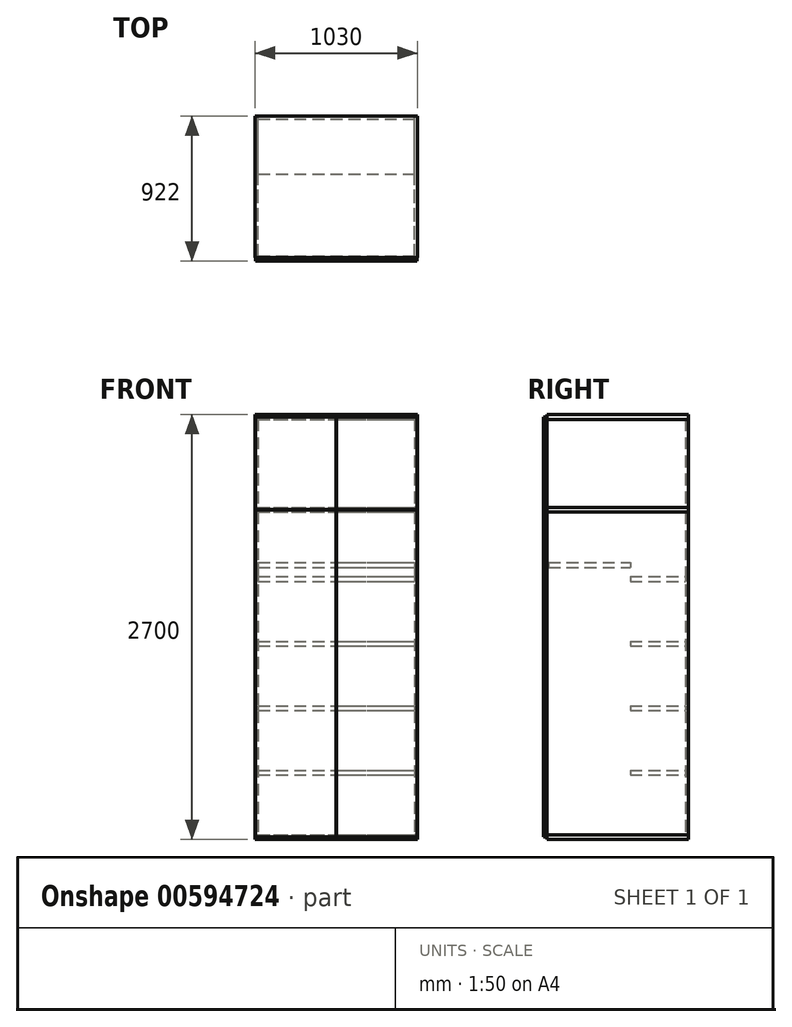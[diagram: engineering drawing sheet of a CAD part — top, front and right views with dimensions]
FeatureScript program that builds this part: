
annotation { "Feature Type Name" : "Feature", "Feature Type Description" : "" }
export const myFeature = defineFeature(function(context is Context, id is Id, definition is map)
    precondition{}
    {
        {
            var Q0;
            Q0=qCreatedBy(makeId("Front.planeOp"),FACE);
            var sketch = newSketch(context, id + "F0", { "sketchPlane" : qUnion([Q0])});
            skLineSegment(sketch, "E0.bottom", {"start": v(515, -1350) * mm, "end": v(-515, -1350) * mm});
            skLineSegment(sketch, "E0.top", {"start": v(515, 1350) * mm, "end": v(-515, 1350) * mm});
            skLineSegment(sketch, "E0.left", {"start": v(515, -1350) * mm, "end": v(515, 1350) * mm});
            skLineSegment(sketch, "E0.right", {"start": v(-515, -1350) * mm, "end": v(-515, 1350) * mm});
            skPoint(sketch, "E0.middle", {"position": v(0, 0) * mm});
            skSolve(sketch);
        }
        {
            var Q0;
            Q0=qCreatedBy(makeId("Front.planeOp"),FACE);
            var sketch = newSketch(context, id + "F1", { "sketchPlane" : qUnion([Q0])});
            skLineSegment(sketch, "E1.bottom", {"start": v(-515, -1350) * mm, "end": v(515, -1350) * mm});
            skLineSegment(sketch, "E1.top", {"start": v(-515, -1320) * mm, "end": v(515, -1320) * mm});
            skLineSegment(sketch, "E1.left", {"start": v(-515, -1350) * mm, "end": v(-515, -1320) * mm});
            skLineSegment(sketch, "E1.right", {"start": v(515, -1350) * mm, "end": v(515, -1320) * mm});
            skLineSegment(sketch, "E2.bottom", {"start": v(-515, 730) * mm, "end": v(515, 730) * mm});
            skLineSegment(sketch, "E2.top", {"start": v(-515, 760) * mm, "end": v(515, 760) * mm});
            skLineSegment(sketch, "E2.left", {"start": v(-515, 730) * mm, "end": v(-515, 760) * mm});
            skLineSegment(sketch, "E2.right", {"start": v(515, 730) * mm, "end": v(515, 760) * mm});
            skLineSegment(sketch, "E3.bottom", {"start": v(-515, 1320) * mm, "end": v(515, 1320) * mm});
            skLineSegment(sketch, "E3.top", {"start": v(-515, 1350) * mm, "end": v(515, 1350) * mm});
            skLineSegment(sketch, "E3.left", {"start": v(-515, 1320) * mm, "end": v(-515, 1350) * mm});
            skLineSegment(sketch, "E3.right", {"start": v(515, 1320) * mm, "end": v(515, 1350) * mm});
            skSolve(sketch);
        }
        {
            var Q0;
            Q0 = qSketchRegion(id + "F1", true);
            extrude(context, id + "F2", {"entities" : qUnion([Q0]), "depth" : 900 * mm, "offsetDistance" : 25 * mm});
        }
        {
            var Q0;
            Q0=qCreatedBy(makeId("Front.planeOp"),FACE);
            var sketch = newSketch(context, id + "F3", { "sketchPlane" : qUnion([Q0])});
            skLineSegment(sketch, "E4", {"start": v(0, 0) * mm, "end": v(0, 1355.76) * mm, "construction": true});
            skLineSegment(sketch, "E5.bottom", {"start": v(-515, 1320) * mm, "end": v(-496, 1320) * mm});
            skLineSegment(sketch, "E5.top", {"start": v(-515, 760) * mm, "end": v(-496, 760) * mm});
            skLineSegment(sketch, "E5.left", {"start": v(-515, 1320) * mm, "end": v(-515, 760) * mm});
            skLineSegment(sketch, "E5.right", {"start": v(-496, 1320) * mm, "end": v(-496, 760) * mm});
            skLineSegment(sketch, "E6.bottom", {"start": v(-515, 730) * mm, "end": v(-496, 730) * mm});
            skLineSegment(sketch, "E6.top", {"start": v(-515, -1320) * mm, "end": v(-496, -1320) * mm});
            skLineSegment(sketch, "E6.left", {"start": v(-515, 730) * mm, "end": v(-515, -1320) * mm});
            skLineSegment(sketch, "E6.right", {"start": v(-496, 730) * mm, "end": v(-496, -1320) * mm});
            skLineSegment(sketch, "E7.MirrorCS", {"start": v(515, -1320) * mm, "end": v(496, -1320) * mm});
            skLineSegment(sketch, "E8.MirrorCS", {"start": v(515, 1320) * mm, "end": v(496, 1320) * mm});
            skLineSegment(sketch, "E9.MirrorCS", {"start": v(515, 760) * mm, "end": v(496, 760) * mm});
            skLineSegment(sketch, "E10.MirrorCS", {"start": v(515, 730) * mm, "end": v(496, 730) * mm});
            skLineSegment(sketch, "E11.MirrorCS", {"start": v(496, 730) * mm, "end": v(496, -1320) * mm});
            skLineSegment(sketch, "E12.MirrorCS", {"start": v(515, 730) * mm, "end": v(515, -1320) * mm});
            skLineSegment(sketch, "E13.MirrorCS", {"start": v(496, 1320) * mm, "end": v(496, 760) * mm});
            skLineSegment(sketch, "E14.MirrorCS", {"start": v(515, 1320) * mm, "end": v(515, 760) * mm});
            skSolve(sketch);
        }
        {
            var Q0;
            Q0 = qSketchRegion(id + "F3", true);
            var Q1;
            Q1=makeQuery(id+"F2.opExtrude","CAP_FACE",FACE,{"disambiguationData":[OSD([sQuery(id+"F1.wireOp",EDGE,"E1.bottom"),sQuery(id+"F1.wireOp",EDGE,"E1.top"),sQuery(id+"F1.wireOp",EDGE,"E1.left"),sQuery(id+"F1.wireOp",EDGE,"E1.right")])],"isStart":false});
            extrude(context, id + "F4", {"entities" : qUnion([Q0]), "endBound" : BoundingType.UP_TO_SURFACE, "depth" : 25 * mm, "endBoundEntityFace" : qUnion([Q1]), "offsetDistance" : 25 * mm});
        }
        {
            var Q0;
            Q0=qCreatedBy(makeId("Front.planeOp"),FACE);
            var sketch = newSketch(context, id + "F5", { "sketchPlane" : qUnion([Q0])});
            skLineSegment(sketch, "E15.bottom", {"start": v(-496, 1320) * mm, "end": v(496, 1320) * mm});
            skLineSegment(sketch, "E15.top", {"start": v(-496, 760) * mm, "end": v(496, 760) * mm});
            skLineSegment(sketch, "E15.left", {"start": v(-496, 1320) * mm, "end": v(-496, 760) * mm});
            skLineSegment(sketch, "E15.right", {"start": v(496, 1320) * mm, "end": v(496, 760) * mm});
            skLineSegment(sketch, "E16.bottom", {"start": v(-496, 730) * mm, "end": v(496, 730) * mm});
            skLineSegment(sketch, "E16.top", {"start": v(-496, -1320) * mm, "end": v(496, -1320) * mm});
            skLineSegment(sketch, "E16.left", {"start": v(-496, 730) * mm, "end": v(-496, -1320) * mm});
            skLineSegment(sketch, "E16.right", {"start": v(496, 730) * mm, "end": v(496, -1320) * mm});
            skSolve(sketch);
        }
        {
            var Q0;
            Q0 = qSketchRegion(id + "F5", true);
            extrude(context, id + "F6", {"entities" : qUnion([Q0]), "depth" : 19 * mm, "offsetDistance" : 25 * mm});
        }
        {
            var Q0;
            Q0=makeQuery(id+"F6.opExtrude","CAP_FACE",FACE,{"disambiguationData":[OSD([sQuery(id+"F5.wireOp",EDGE,"E16.bottom"),sQuery(id+"F5.wireOp",EDGE,"E16.top"),sQuery(id+"F5.wireOp",EDGE,"E16.left"),sQuery(id+"F5.wireOp",EDGE,"E16.right")])],"isStart":false});
            var sketch = newSketch(context, id + "F7", { "sketchPlane" : qUnion([Q0])});
            skLineSegment(sketch, "E17.bottom", {"start": v(-496, -910) * mm, "end": v(496, -910) * mm});
            skLineSegment(sketch, "E17.top", {"start": v(-496, -940) * mm, "end": v(496, -940) * mm});
            skLineSegment(sketch, "E17.left", {"start": v(-496, -910) * mm, "end": v(-496, -940) * mm});
            skLineSegment(sketch, "E17.right", {"start": v(496, -910) * mm, "end": v(496, -940) * mm});
            skLineSegment(sketch, "E18.0.1.0", {"start": v(-496, -530) * mm, "end": v(496, -530) * mm});
            skLineSegment(sketch, "E18.0.1.1", {"start": v(-496, -500) * mm, "end": v(496, -500) * mm});
            skLineSegment(sketch, "E18.0.1.2", {"start": v(496, -500) * mm, "end": v(496, -530) * mm});
            skLineSegment(sketch, "E18.0.1.3", {"start": v(-496, -500) * mm, "end": v(-496, -530) * mm});
            skLineSegment(sketch, "E18.0.2.0", {"start": v(-496, -120) * mm, "end": v(496, -120) * mm});
            skLineSegment(sketch, "E18.0.2.1", {"start": v(-496, -90) * mm, "end": v(496, -90) * mm});
            skLineSegment(sketch, "E18.0.2.2", {"start": v(496, -90) * mm, "end": v(496, -120) * mm});
            skLineSegment(sketch, "E18.0.2.3", {"start": v(-496, -90) * mm, "end": v(-496, -120) * mm});
            skLineSegment(sketch, "E18.0.3.0", {"start": v(-496, 290) * mm, "end": v(496, 290) * mm});
            skLineSegment(sketch, "E18.0.3.1", {"start": v(-496, 320) * mm, "end": v(496, 320) * mm});
            skLineSegment(sketch, "E18.0.3.2", {"start": v(496, 320) * mm, "end": v(496, 290) * mm});
            skLineSegment(sketch, "E18.0.3.3", {"start": v(-496, 320) * mm, "end": v(-496, 290) * mm});
            skLineSegment(sketch, "E18.direction1", {"start": v(-496, -940) * mm, "end": v(-471, -940) * mm, "construction": true});
            skLineSegment(sketch, "E18.direction2", {"start": v(-496, -940) * mm, "end": v(-496, -530) * mm, "construction": true});
            skSolve(sketch);
        }
        {
            var Q0;
            Q0 = qSketchRegion(id + "F7", true);
            extrude(context, id + "F8", {"entities" : qUnion([Q0]), "depth" : 350 * mm, "offsetDistance" : 25 * mm});
        }
        {
            var Q0;
            Q0=makeQuery(id+"F8.opExtrude","CAP_FACE",FACE,{"disambiguationData":[OSD([sQuery(id+"F7.wireOp",EDGE,"E18.0.3.0"),sQuery(id+"F7.wireOp",EDGE,"E18.0.3.1"),sQuery(id+"F7.wireOp",EDGE,"E18.0.3.2"),sQuery(id+"F7.wireOp",EDGE,"E18.0.3.3")])],"isStart":false});
            var sketch = newSketch(context, id + "F9", { "sketchPlane" : qUnion([Q0])});
            skLineSegment(sketch, "E19.bottom", {"start": v(-496, 410) * mm, "end": v(496, 410) * mm});
            skLineSegment(sketch, "E19.top", {"start": v(-496, 380) * mm, "end": v(496, 380) * mm});
            skLineSegment(sketch, "E19.left", {"start": v(-496, 410) * mm, "end": v(-496, 380) * mm});
            skLineSegment(sketch, "E19.right", {"start": v(496, 410) * mm, "end": v(496, 380) * mm});
            skSolve(sketch);
        }
        {
            var Q0;
            Q0 = qSketchRegion(id + "F9", true);
            extrude(context, id + "F10", {"entities" : qUnion([Q0]), "depth" : 520 * mm, "offsetDistance" : 25 * mm});
        }
        {
            var Q0;
            Q0=makeQuery(id+"F4.opExtrude","CAP_FACE",FACE,{"disambiguationData":[OSD([sQuery(id+"F3.wireOp",EDGE,"E6.bottom"),sQuery(id+"F3.wireOp",EDGE,"E6.top"),sQuery(id+"F3.wireOp",EDGE,"E6.left"),sQuery(id+"F3.wireOp",EDGE,"E6.right")])],"isStart":false});
            var sketch = newSketch(context, id + "F11", { "sketchPlane" : qUnion([Q0])});
            skLineSegment(sketch, "E20", {"start": v(0, 0) * mm, "end": v(0, -429.81) * mm, "construction": true});
            skLineSegment(sketch, "E21.bottom", {"start": v(-513, 744) * mm, "end": v(-0.5, 744) * mm});
            skLineSegment(sketch, "E21.top", {"start": v(-513, -1334) * mm, "end": v(-0.5, -1334) * mm});
            skLineSegment(sketch, "E21.left", {"start": v(-513, 744) * mm, "end": v(-513, -1334) * mm});
            skLineSegment(sketch, "E21.right", {"start": v(-0.5, 744) * mm, "end": v(-0.5, -1334) * mm});
            skLineSegment(sketch, "E22.bottom", {"start": v(-513, 1334) * mm, "end": v(-0.5, 1334) * mm});
            skLineSegment(sketch, "E22.top", {"start": v(-513, 746) * mm, "end": v(-0.5, 746) * mm});
            skLineSegment(sketch, "E22.left", {"start": v(-513, 1334) * mm, "end": v(-513, 746) * mm});
            skLineSegment(sketch, "E22.right", {"start": v(-0.5, 1334) * mm, "end": v(-0.5, 746) * mm});
            skLineSegment(sketch, "E23.MirrorCS", {"start": v(513, 744) * mm, "end": v(0.5, 744) * mm});
            skLineSegment(sketch, "E24.MirrorCS", {"start": v(513, -1334) * mm, "end": v(0.5, -1334) * mm});
            skLineSegment(sketch, "E25.MirrorCS", {"start": v(513, 744) * mm, "end": v(513, -1334) * mm});
            skLineSegment(sketch, "E26.MirrorCS", {"start": v(0.5, 1334) * mm, "end": v(0.5, 746) * mm});
            skLineSegment(sketch, "E27.MirrorCS", {"start": v(513, 1334) * mm, "end": v(513, 746) * mm});
            skLineSegment(sketch, "E28.MirrorCS", {"start": v(513, 746) * mm, "end": v(0.5, 746) * mm});
            skLineSegment(sketch, "E29.MirrorCS", {"start": v(513, 1334) * mm, "end": v(0.5, 1334) * mm});
            skLineSegment(sketch, "E30.MirrorCS", {"start": v(0.5, 744) * mm, "end": v(0.5, -1334) * mm});
            skSolve(sketch);
        }
        {
            var Q0;
            Q0 = qSketchRegion(id + "F11", true);
            extrude(context, id + "F12", {"entities" : qUnion([Q0]), "depth" : 22 * mm, "offsetDistance" : 25 * mm});
        }
    });
